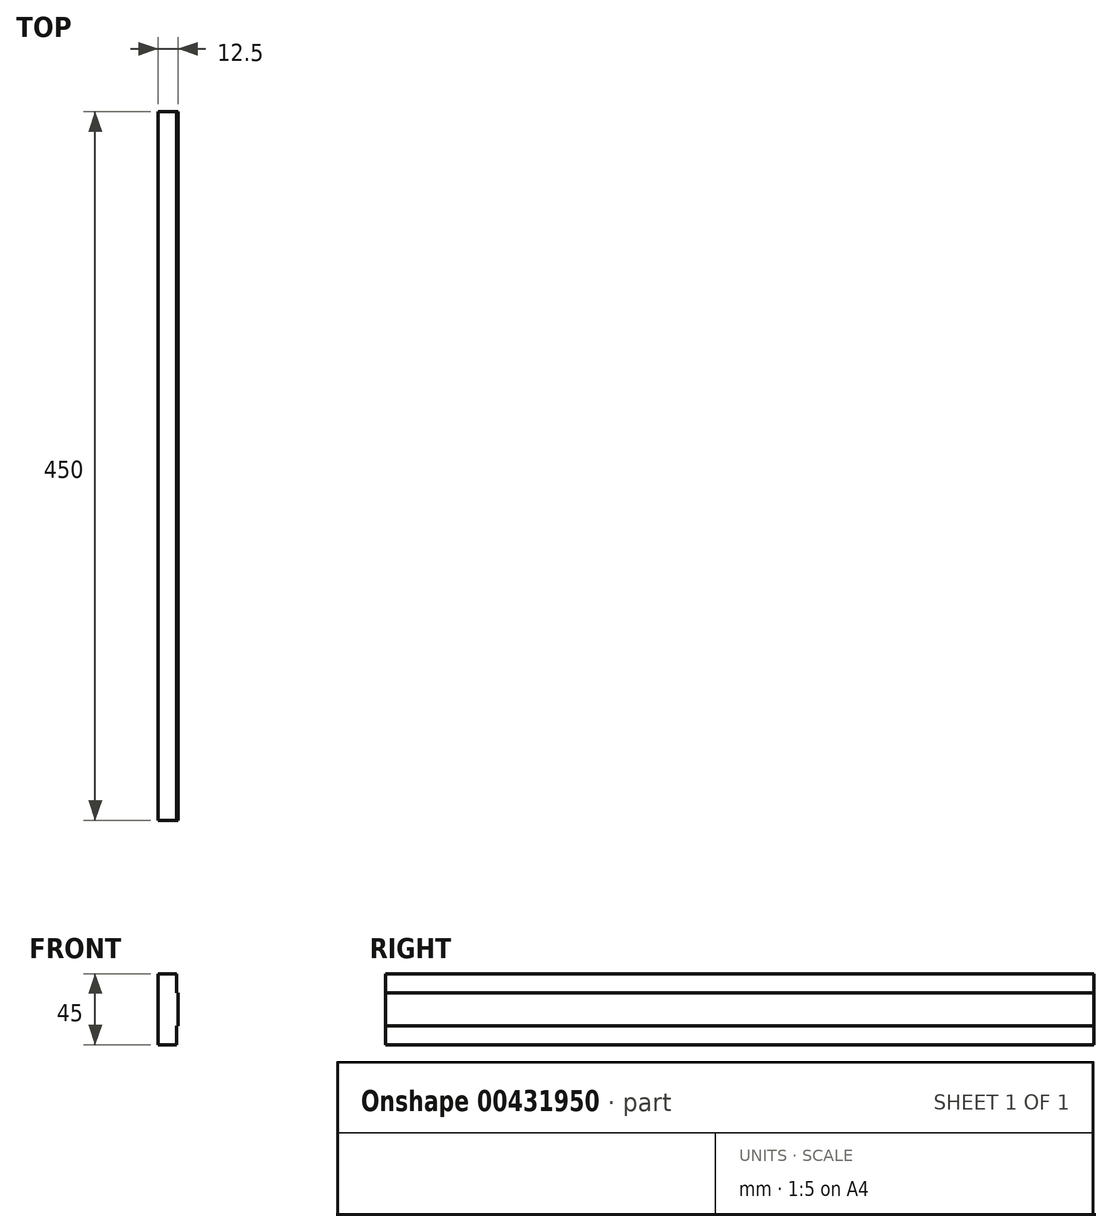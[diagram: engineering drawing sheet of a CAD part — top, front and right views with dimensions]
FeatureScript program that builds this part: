
annotation { "Feature Type Name" : "Feature", "Feature Type Description" : "" }
export const myFeature = defineFeature(function(context is Context, id is Id, definition is map)
    precondition{}
    {
        {
            var Q0;
            Q0=qCreatedBy(makeId("Right.planeOp"),FACE);
            var sketch = newSketch(context, id + "F0", { "sketchPlane" : qUnion([Q0])});
            skLineSegment(sketch, "E0.bottom", {"start": v(0, 0) * mm, "end": v(-450, 0) * mm});
            skLineSegment(sketch, "E0.top", {"start": v(0, 45) * mm, "end": v(-450, 45) * mm});
            skLineSegment(sketch, "E0.left", {"start": v(0, 0) * mm, "end": v(0, 45) * mm});
            skLineSegment(sketch, "E0.right", {"start": v(-450, 0) * mm, "end": v(-450, 45) * mm});
            skSolve(sketch);
        }
        {
            var Q0;
            Q0 = qSketchRegion(id + "F0", true);
            extrude(context, id + "F1", {"entities" : qUnion([Q0]), "depth" : 12.5 * mm, "offsetDistance" : 25 * mm});
        }
        {
            var Q0;
            Q0=makeQuery(id+"F1.opExtrude","CAP_FACE",FACE,{"disambiguationData":[OSD([sQuery(id+"F0.wireOp",EDGE,"E0.bottom"),sQuery(id+"F0.wireOp",EDGE,"E0.top"),sQuery(id+"F0.wireOp",EDGE,"E0.left"),sQuery(id+"F0.wireOp",EDGE,"E0.right")])],"isStart":false});
            var sketch = newSketch(context, id + "F2", { "sketchPlane" : qUnion([Q0])});
            skLineSegment(sketch, "E1.bottom", {"start": v(-450, 45) * mm, "end": v(0, 45) * mm});
            skLineSegment(sketch, "E1.top", {"start": v(-450, 33) * mm, "end": v(0, 33) * mm});
            skLineSegment(sketch, "E1.left", {"start": v(-450, 45) * mm, "end": v(-450, 33) * mm});
            skLineSegment(sketch, "E1.right", {"start": v(0, 45) * mm, "end": v(0, 33) * mm});
            skLineSegment(sketch, "E2.bottom", {"start": v(-450, 0) * mm, "end": v(0, 0) * mm});
            skLineSegment(sketch, "E2.top", {"start": v(-450, 12) * mm, "end": v(0, 12) * mm});
            skLineSegment(sketch, "E2.left", {"start": v(-450, 0) * mm, "end": v(-450, 12) * mm});
            skLineSegment(sketch, "E2.right", {"start": v(0, 0) * mm, "end": v(0, 12) * mm});
            skSolve(sketch);
        }
        {
            var Q0;
            Q0 = qSketchRegion(id + "F2", true);
            extrude(context, id + "F3", {"entities" : qUnion([Q0]), "operationType" : NewBodyOperationType.REMOVE, "oppositeDirection" : true, "depth" : 1 * mm, "offsetDistance" : 25 * mm});
        }
    });
